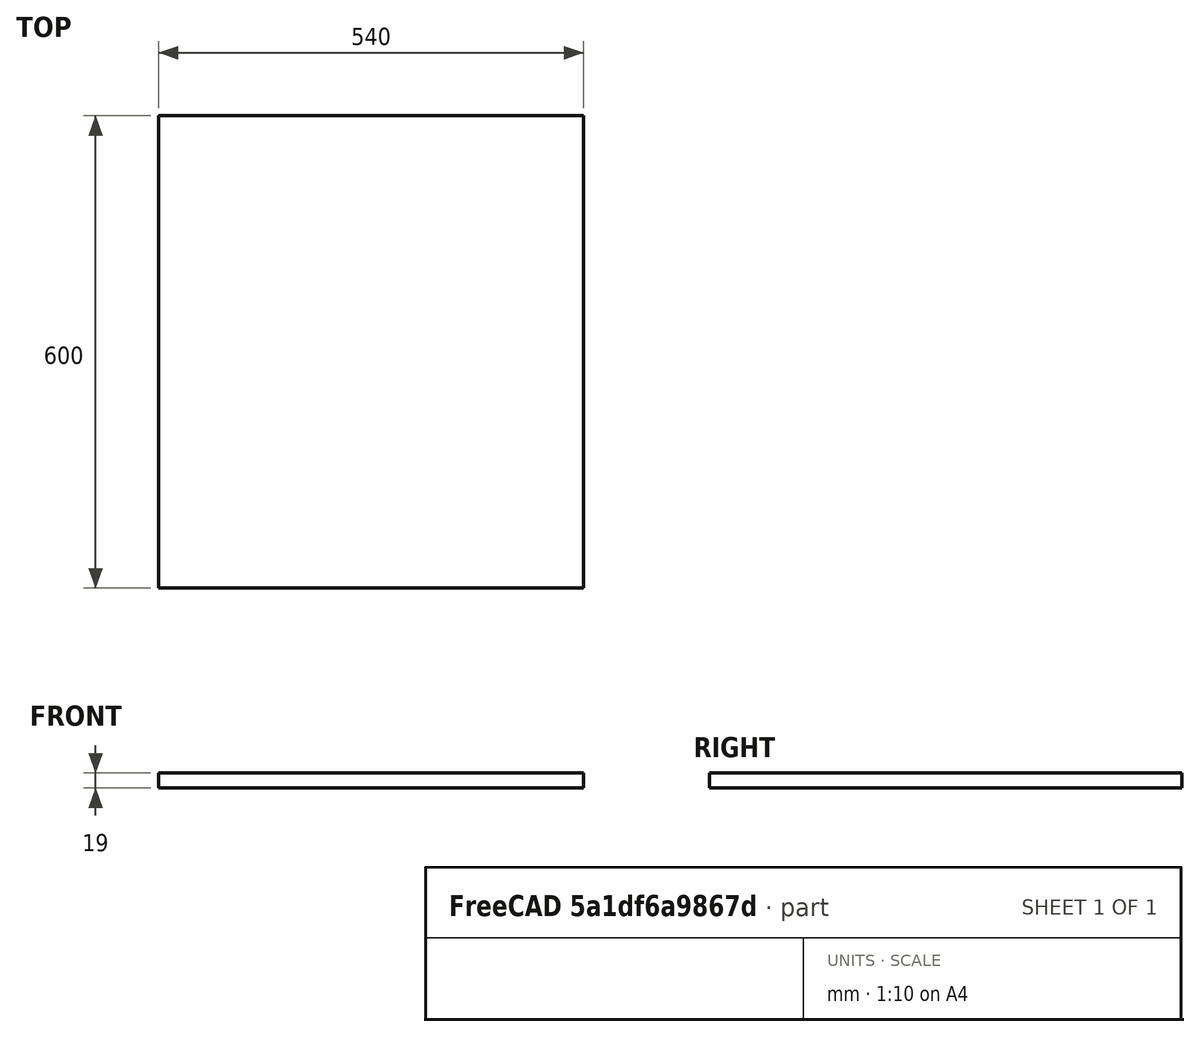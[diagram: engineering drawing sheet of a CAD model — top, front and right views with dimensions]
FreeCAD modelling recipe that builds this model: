
FCSTD DOCUMENT  (FreeCAD 1.0RUnknown)
Label: wardrobe_top_jan
License: All rights reserved
LicenseURL: https://en.wikipedia.org/wiki/All_rights_reserved
objects: Sketcher::SketchObject×1, PartDesign::Pad×1, PartDesign::CoordinateSystem×1, PartDesign::Body×1
note: 7 computed .brp shape members not serialized (recipe doc carries the construction recipe); baked Part::Feature solids carry a one-line shape summary decoded from their .brp
EXTERNAL_REF file=../../mastersketch.FCStd obj=Spreadsheet

FEATURE [Sketcher::SketchObject] Sketch003
  ArcFitTolerance = 1e-06
  AttachmentSupport = -> [XY_Plane005]
  FullyConstrained = true
  MakeInternals = false
  MapMode = 5
  expr: Constraints[10] = mastersketch#Spreadsheet.corpus_width
  expr: Constraints[11] = mastersketch#Spreadsheet.corpus_depth
  sketch-geometry (5):
    g0: LineSegment StartX=-270 StartY=-300 StartZ=0 EndX=270 EndY=-300 EndZ=0
    g1: LineSegment StartX=270 StartY=-300 StartZ=0 EndX=270 EndY=300 EndZ=0
    g2: LineSegment StartX=270 StartY=300 StartZ=0 EndX=-270 EndY=300 EndZ=0
    g3: LineSegment StartX=-270 StartY=300 StartZ=0 EndX=-270 EndY=-300 EndZ=0
    g4: GeomPoint [constr] X=0 Y=0 Z=0
  constraints (12):
    c: Coincident(g0,g1)
    c: Coincident(g1,g2)
    c: Coincident(g2,g3)
    c: Coincident(g3,g0)
    c: Horizontal(g0)
    c: Horizontal(g2)
    c: Vertical(g1)
    c: Vertical(g3)
    c: Symmetric(g2,g0,g4)
    c: Coincident(g4,g-1)
    c: DistanceX(g0,g0) = 540
    c: DistanceY(g3,g3) = 600
FEATURE [PartDesign::Pad] Pad003
  Direction = (0,0,1)
  Length = 19
  Length2 = 10
  Profile = -> Sketch003
  ReferenceAxis = -> Sketch003 [N_Axis]
  Refine = true
  Suppressed = false
  Type = 0
  expr: Length = mastersketch#Spreadsheet.corpus_outer_thickness
FEATURE [PartDesign::CoordinateSystem] LCS_left
  AttacherType = Attacher::AttachEngine3D
  AttachmentSupport = -> [Pad003]
  MapMode = 45
  Placement = pos=(-270,1.42e-14,0) rot=(0,0.707107,0.707107;3.14159rad)
FEATURE [PartDesign::Body] Body003  label="wardrobe_top_jan"
  AllowCompound = false
  Group = -> [Sketch003,Pad003,LCS_left]
  Origin = -> Origin005
  Tip = -> Pad003
